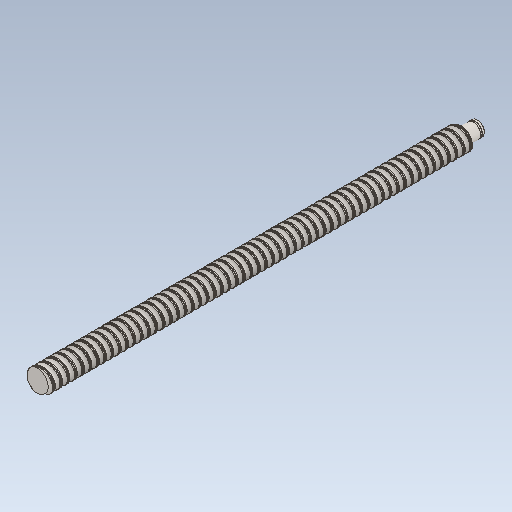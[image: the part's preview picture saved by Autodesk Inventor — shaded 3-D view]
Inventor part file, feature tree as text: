
AUTODESK INVENTOR PART (.ipt)
format: ipt  version: 2020.1 (Build 241239000, 239)  size: 3,649,536 bytes
history: native  units: mm
features: other x2, extrude x1, sketch x1
ambient origin geometry x8: Origin, YZ Plane, XZ Plane, XY Plane, X Axis, Y Axis, Z Axis, Center Point
bodies: Body1 (feature_tree)
feature tree (4):
  other  "Твердое тело1"
  extrude  "Выдавливание1"  Depth=100.0mm TaperAngle=0.0deg
  sketch  "Эскиз1"
  other  "Aesthetic Chamfer"
